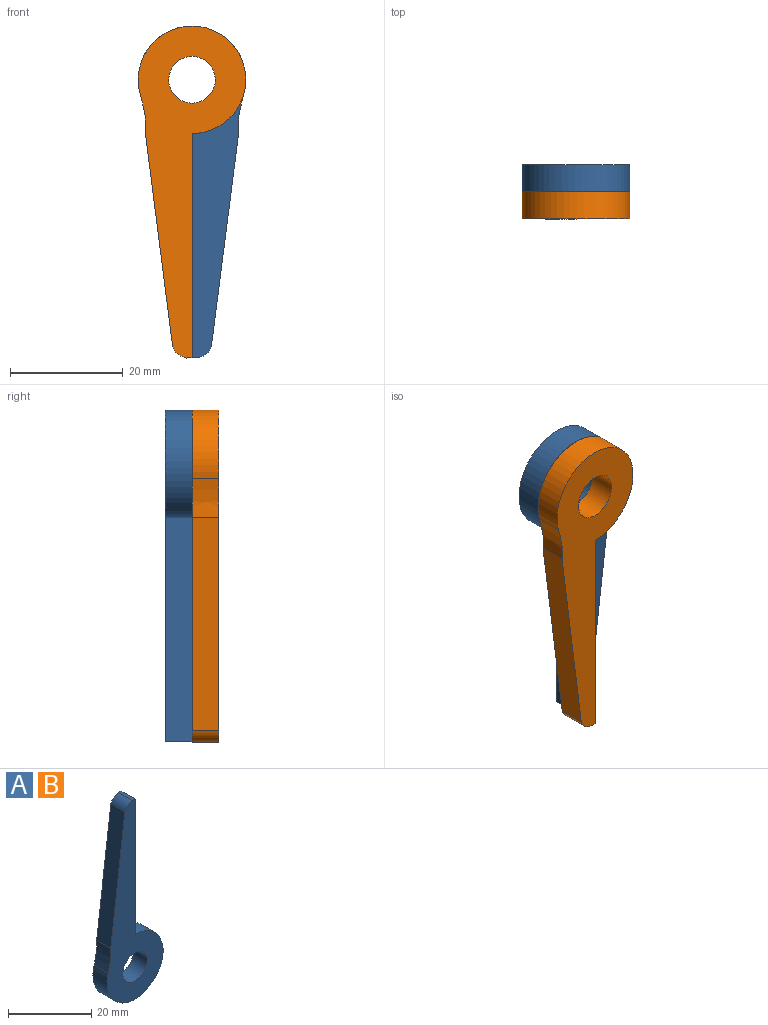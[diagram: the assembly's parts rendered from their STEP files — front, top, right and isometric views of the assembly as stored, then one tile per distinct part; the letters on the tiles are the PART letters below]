
ASSEMBLY  parts=2 mates=1
PART A: 9 faces, bbox 19.1x4.8x58.8 mm
  f0: plane 37.78x4.83mm, normal (-0.99,0,0.13), area 181.4mm2, adj f1,f5,f7,f8
  f1: extruded ~6.88x4.76mm, area 33.2mm2, adj f0,f2,f7,f8
  f2: cylinder r=9.53mm len=19.05mm, axis (0,1,0), area 226.5mm2, adj f1,f3,f7,f8
  f3: plane 39.76x4.76mm, normal (1,0,0), area 189.3mm2, adj f2,f4,f7,f8
  f4: plane 4.76x0.95mm, normal (0,0,1), area 4.5mm2, adj f3,f5,f7,f8
  f5: cylinder r=3.17mm len=4.76mm, axis (0,1,0), area 15.8mm2, adj f0,f4,f7,f8
  f6: cylinder r=4.13mm len=8.26mm, axis (0,1,0), area 123.5mm2, adj f7,f8
  f7: plane 58.81x19.05mm, normal (0,-1,0), area 469.4mm2, adj f0,f1,f2,f3,f4,f5,f6
  f8: plane 58.81x19.05mm, normal (0,1,0), area 469.4mm2, adj f0,f1,f2,f3,f4,f5,f6
PART B: same geometry as A
PLACE A rot(axis=(0,1,0),180deg) t=(18.99,1.91,28.29)mm
PLACE B rot(axis=(1,0,0),180deg) t=(18.99,-7.62,28.29)mm
MATE revolute A.f6 <-> B.f6  axis (0,-1,0) through (18.99,-2.86,28.29)mm
